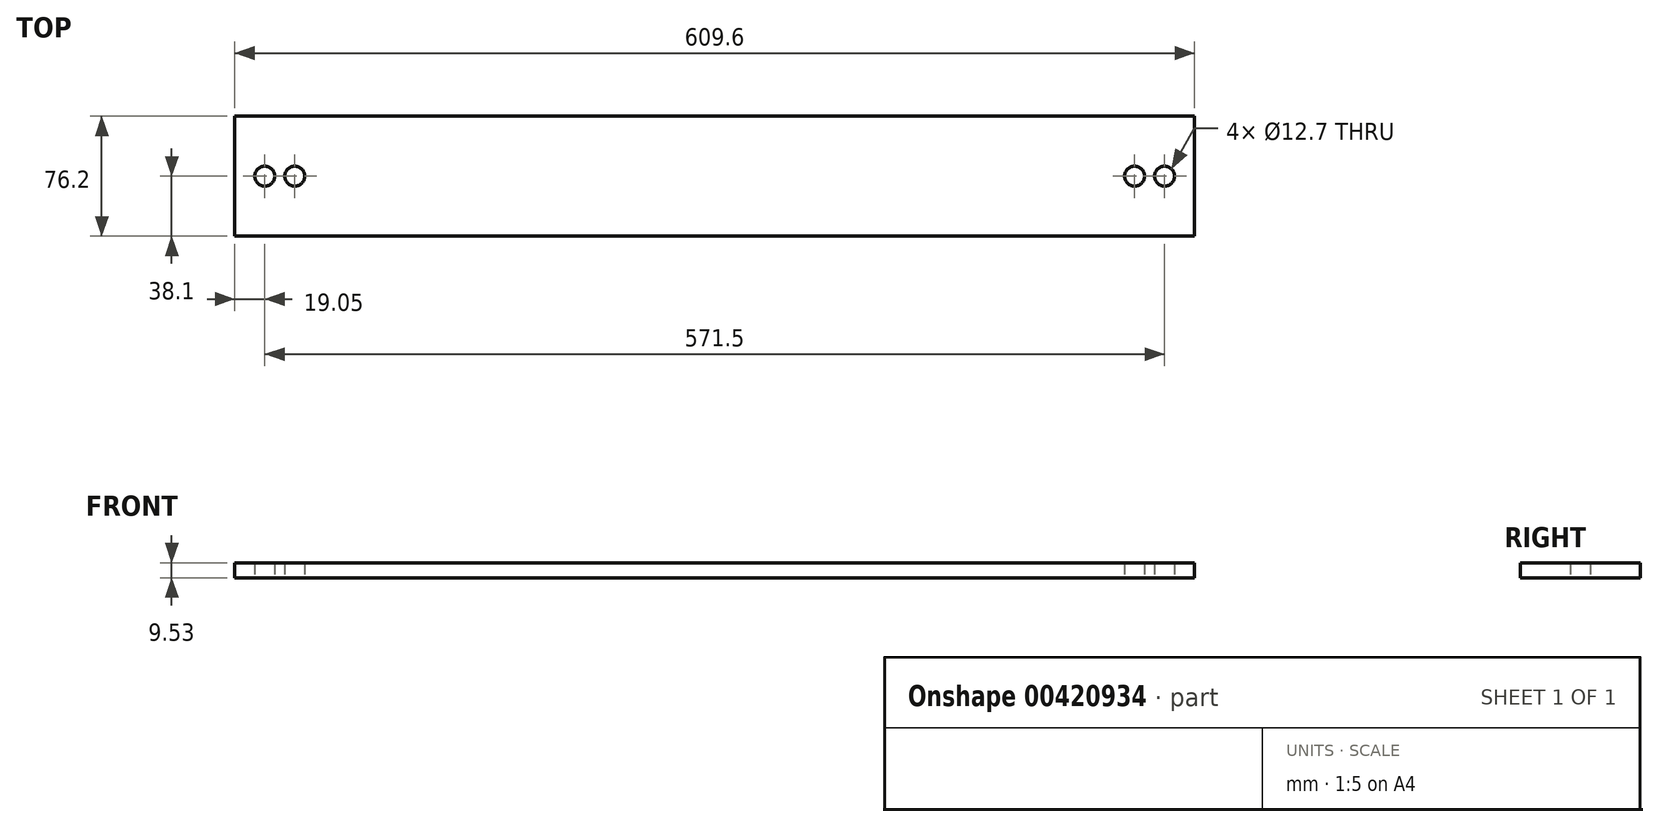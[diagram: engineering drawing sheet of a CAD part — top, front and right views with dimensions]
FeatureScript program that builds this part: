
annotation { "Feature Type Name" : "Feature", "Feature Type Description" : "" }
export const myFeature = defineFeature(function(context is Context, id is Id, definition is map)
    precondition{}
    {
        {
            var Q0;
            Q0=qCreatedBy(makeId("Top.planeOp"),FACE);
            var sketch = newSketch(context, id + "F0", { "sketchPlane" : qUnion([Q0])});
            skLineSegment(sketch, "E0.bottom", {"start": v(0, 0) * mm, "end": v(609.6, 0) * mm});
            skLineSegment(sketch, "E0.top", {"start": v(0, -76.2) * mm, "end": v(609.6, -76.2) * mm});
            skLineSegment(sketch, "E0.left", {"start": v(0, 0) * mm, "end": v(0, -76.2) * mm});
            skLineSegment(sketch, "E0.right", {"start": v(609.6, 0) * mm, "end": v(609.6, -76.2) * mm});
            skCircle(sketch, "E1", {"center": v(19.05, -38.1) * mm, "radius": 6.35 * mm});
            skCircle(sketch, "E2", {"center": v(38.1, -38.1) * mm, "radius": 6.35 * mm});
            skCircle(sketch, "E3", {"center": v(571.5, -38.1) * mm, "radius": 6.35 * mm});
            skCircle(sketch, "E4", {"center": v(590.55, -38.1) * mm, "radius": 6.35 * mm});
            skPoint(sketch, "E5", {"position": v(0, -38.1) * mm});
            skSolve(sketch);
        }
        {
            var Q0;
            Q0=qSketchRegion(id+"F0",true);
            extrude(context, id + "F1", {"entities" : qUnion([Q0]), "depth" : 9.52 * mm});
        }
    });
